# Revit family: 32_Mx1020001_Grifería de Mesa Push Max
name_source: partatom
category: Aparatos sanitarios
revit_build: Autodesk Revit 2018 (Build: 20170223_1515(x64)
units: mm (PartAtom-declared; Revit-internal decimal feet)

## family parameters
Anfitrión = Cara
Compartido = No
Corte con vacíos al cargar = No
Cota de conector redondo = Diámetro de uso
Número OmniClass = 23.45.55.14
Punto de cálculo de habitación = No
Tipo de pieza = Normal
Título OmniClass = Single Faucets

## types (1)
- 32_Mx1020001_Grifería de Mesa Push Max
    Accionamiento = Push
    Caudal = 1.5 l/min (60 psi)
    Consumo de Agua = 195 ml por ciclo
    Cumple Edge = Si
    Cumple Leed = Si
    Código de montaje = D2010300
    Diametros de conexión = 1/2 pulg. NPSM
    Elevación por defecto = 0 mm  [stored 0 ft]
    Garantía = Garantía de 3 años por defectos de fabricación y cromados.
    Marca = Corona
    Material = Latón
    Material Acabado = Cromo_CORONA
    Nombre = Grifería de Mesa Push Max
    Presión Máxima = 80 PSI
    Presión Mínima = 14.5 PSI
    Referencia = Mx1020001
    Tipo = Grifería Lavamanos
    Tráfico = Institucional Alto tráfico
    URL = https://www.corona.co
    Vida Util ( Ciclos ) = 150000

note: [stored X ft] marks values corroborated as IEEE doubles in the binary element streams (Revit-internal decimal feet)
